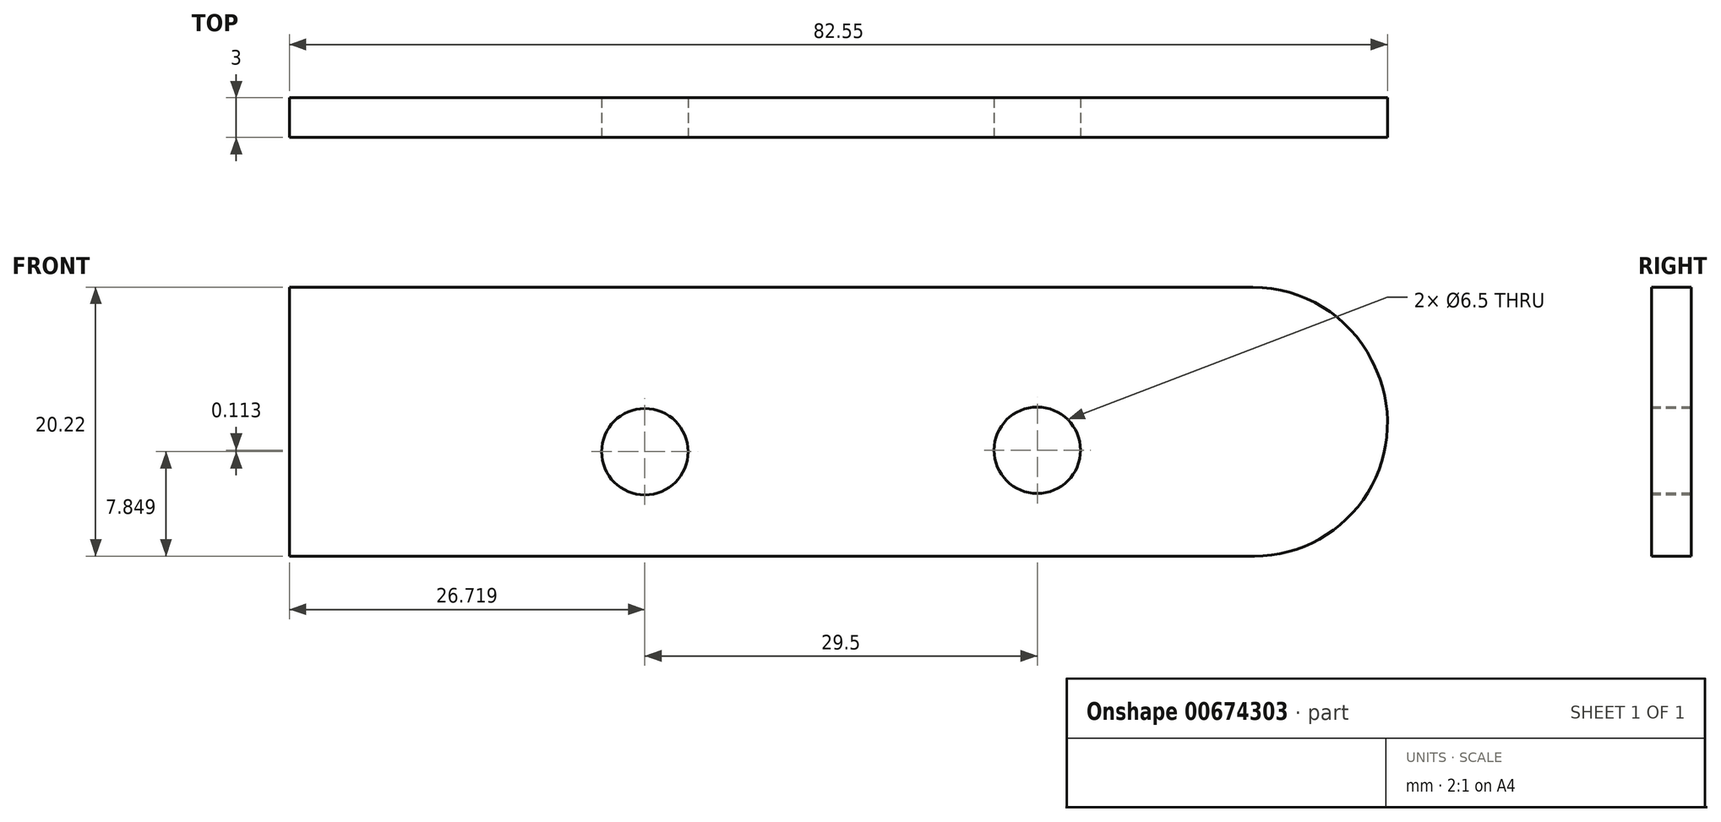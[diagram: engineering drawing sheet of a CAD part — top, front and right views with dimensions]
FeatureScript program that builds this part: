
annotation { "Feature Type Name" : "Feature", "Feature Type Description" : "" }
export const myFeature = defineFeature(function(context is Context, id is Id, definition is map)
    precondition{}
    {
        {
            var Q0;
            Q0=qCreatedBy(makeId("Front.planeOp"),FACE);
            var sketch = newSketch(context, id + "F0", { "sketchPlane" : qUnion([Q0])});
            skLineSegment(sketch, "E0.bottom", {"start": v(-19.98, 6.18) * mm, "end": v(52.45, 6.18) * mm});
            skLineSegment(sketch, "E0.top", {"start": v(-19.98, -14.04) * mm, "end": v(52.57, -14.04) * mm});
            skLineSegment(sketch, "E0.right", {"start": v(61.38, 0.7) * mm, "end": v(61.5, 0.47) * mm});
            skPoint(sketch, "E1.visualSharp", {"position": v(58.6, 6.18) * mm});
            skArc(sketch, "E1.filletArc", {"start": v(61.38, 0.7) * mm, "mid": v(57.7, 4.7) * mm, "end": v(52.45, 6.18) * mm});
            skPoint(sketch, "E2.visualSharp", {"position": v(68.83, -14.04) * mm});
            skArc(sketch, "E2.filletArc", {"start": v(52.57, -14.04) * mm, "mid": v(61.08, -9.28) * mm, "end": v(61.5, 0.47) * mm});
            skPoint(sketch, "E0.left.start.orphan", {"position": v(-31.4, 6.18) * mm});
            skLineSegment(sketch, "E3", {"start": v(-19.98, 6.18) * mm, "end": v(-19.98, -14.04) * mm});
            skSolve(sketch);
        }
        {
            var Q0;
            Q0 = qSketchRegion(id + "F0", true);
            extrude(context, id + "F1", {"entities" : qUnion([Q0]), "depth" : 3 * mm, "offsetDistance" : 25 * mm});
        }
        {
            var Q0;
            Q0=makeQuery(id+"F1.opExtrude","CAP_FACE",FACE,{"disambiguationData":[OSD([sQuery(id+"F0.wireOp",EDGE,"E0.bottom"),sQuery(id+"F0.wireOp",EDGE,"E0.top"),sQuery(id+"F0.wireOp",EDGE,"E0.right"),sQuery(id+"F0.wireOp",EDGE,"E1.filletArc"),sQuery(id+"F0.wireOp",EDGE,"E2.filletArc"),sQuery(id+"F0.wireOp",EDGE,"E3")])],"isStart":false});
            var sketch = newSketch(context, id + "F2", { "sketchPlane" : qUnion([Q0])});
            skPoint(sketch, "E4", {"position": v(36.24, -6.08) * mm});
            skPoint(sketch, "E5", {"position": v(6.74, -6.2) * mm});
            skSolve(sketch);
        }
        {
            var Q0;
            Q0=sQuery(id+"F2.wireOp",VERTEX,"dc8834ab-6140-452a-a872-a296b9bf9db7");
            var Q1;
            Q1=sQuery(id+"F2.wireOp",VERTEX,"E4");
            var Q2;
            Q2=sQuery(id+"F2.wireOp",VERTEX,"E5");
            var Q3;
            Q3=makeQuery(id+"F1.opExtrude","SWEPT_BODY",BODY,{"disambiguationData":[OSD([sQuery(id+"F0.wireOp",EDGE,"E0.bottom"),sQuery(id+"F0.wireOp",EDGE,"E0.top"),sQuery(id+"F0.wireOp",EDGE,"E0.right"),sQuery(id+"F0.wireOp",EDGE,"E1.filletArc"),sQuery(id+"F0.wireOp",EDGE,"E2.filletArc"),sQuery(id+"F0.wireOp",EDGE,"E3")])]});
            hole(context, id + "F3", {"style" : HoleStyle.C_BORE, "endStyle" : HoleEndStyle.BLIND, "standardTappedOrClearance" : lookupTablePath({ "standard" : "ISO", "fit" : "Normal", "size" : "M3", "type" : "Clearance" }), "standardBlindInLast" : lookupTablePath({ "fit" : "Standard", "standard" : "ISO", "size" : "M3", "type" : "Clearance" }), "holeDiameter" : 3.3 * mm, "cBoreDiameter" : 6.5 * mm, "cBoreDepth" : 3 * mm, "majorDiameter" : 5 * mm, "holeDepth" : 14.4 * mm, "isTappedThrough" : true, "tappedDepth" : 12 * mm, "tapClearance" : 3, "startFromSketch" : true, "locations" : qUnion([Q0, Q1, Q2]), "scope" : qUnion([Q3])});
        }
    });
